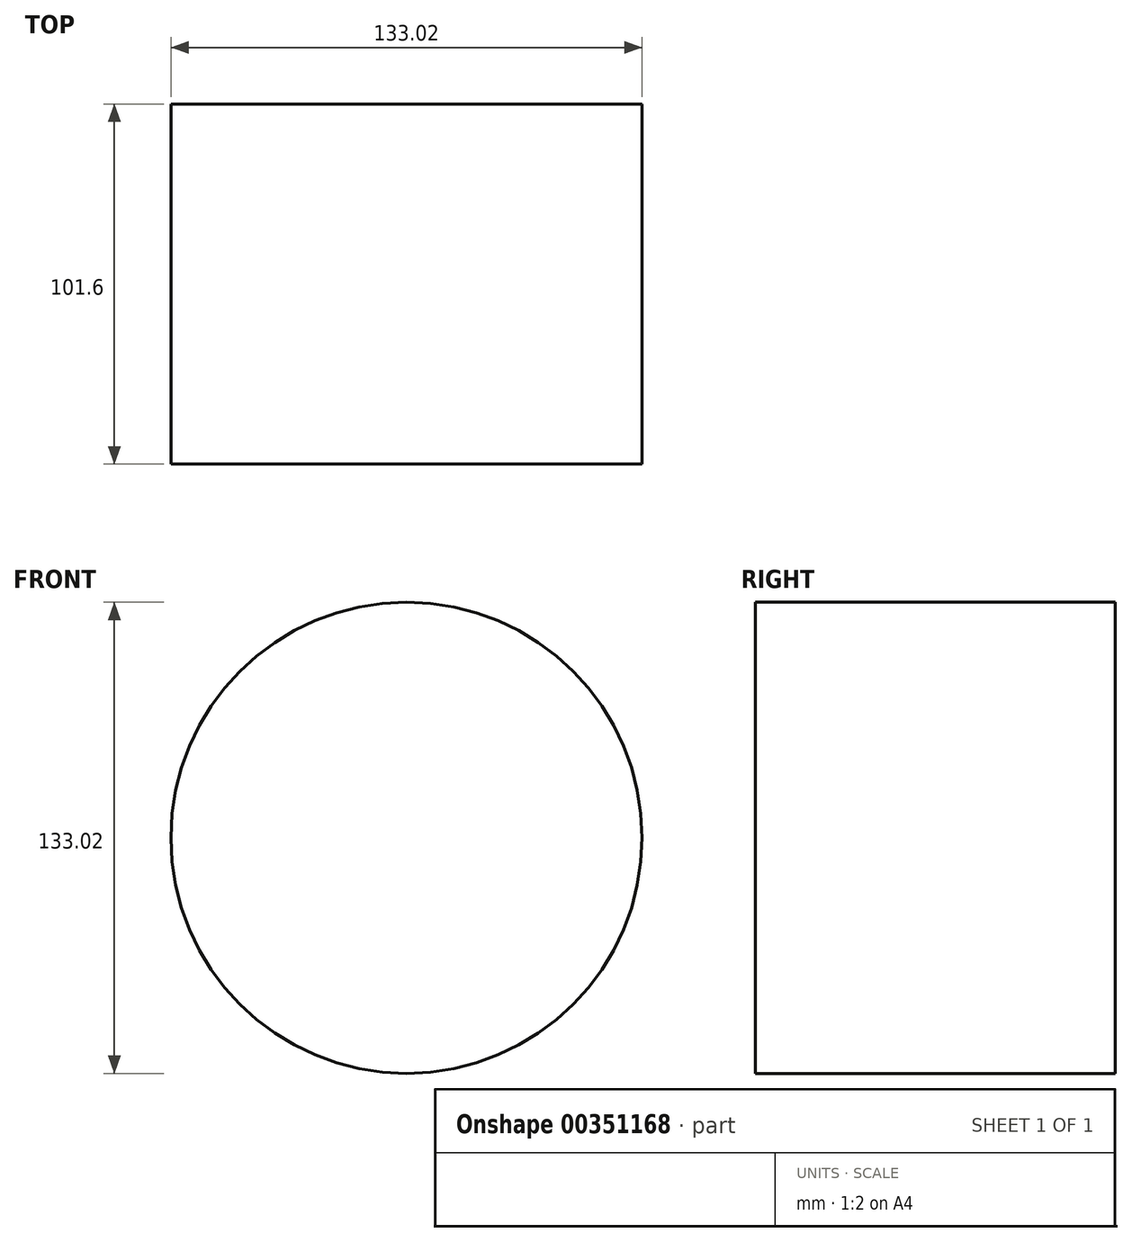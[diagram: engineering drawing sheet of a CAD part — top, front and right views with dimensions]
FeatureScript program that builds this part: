
annotation { "Feature Type Name" : "Feature", "Feature Type Description" : "" }
export const myFeature = defineFeature(function(context is Context, id is Id, definition is map)
    precondition{}
    {
        {
            var Q0;
            Q0=qCreatedBy(makeId("Front.planeOp"),FACE);
            var sketch = newSketch(context, id + "F0", { "sketchPlane" : qUnion([Q0])});
            skCircle(sketch, "E0", {"center": v(0, 0) * mm, "radius": 66.5 * mm});
            skSolve(sketch);
        }
        {
            var Q0;
            Q0=makeQuery(id+"F0.imprint","IMPRINT",FACE,{"disambiguationData":[TD([[makeQuery(id+"F0.imprint","IMPRINT",EDGE,{"derivedFrom":sQuery(id+"F0.wireOp",EDGE,"E0")}),1.0]])]});
            extrude(context, id + "F1", {"entities" : qUnion([Q0]), "endBound" : BoundingType.SYMMETRIC, "depth" : 101.6 * mm});
        }
    });
